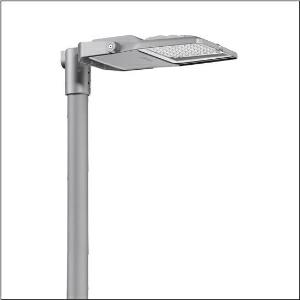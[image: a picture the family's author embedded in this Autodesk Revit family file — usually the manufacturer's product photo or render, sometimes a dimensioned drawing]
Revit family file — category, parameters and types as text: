
# Revit family: floodlight_fl_21_iq_mini___pl64_5xa7772b2e3a_76f3
name_source: partatom
category: Lighting Fixtures
units: mm (PartAtom-declared; Revit-internal decimal feet)

## family parameters
Cut with Voids When Loaded = No
Host = Face
Light Source = No
Part Type = Normal
Room Calculation Point = No
Round Connector Dimension = Use Diameter
Shared = No

## types (1)
- --- (1 x LED, 6020 lm, 45.5 W, 3000K)
    Apparent Load = 46 VA
    CIE Flux Codes = 28 80 98 100 100
    Color Rendering = 70
    Color Temperature = 3000K
    Default Elevation = 1800 mm
    Description = Floodlight FL 21 iQ mini, floodlight, primary light control with lens, of PMMA, primary optical cover: protective disc, of toughened safety glass, transparent, light distribution: PL64, light emission: direct distribution, installation type: surface-mounted, LED, High Power LED, rated luminous flux: 6.020lm, luminous efficacy: 132lm/W, light colour: 730, colour temperature: 3000K, control: Auto-Match, Temp-Guard, Night-Set, Smart-Wire, Desk-Remote (wireless, voltage-free reading and setting of iQ features in the workshop via application-optimized NFC function/RFID function), optimised constant luminous flux control (CLO 2.0), Light-Fading, Lumen-Switch, with terminal, 6-pole, mains connection: 220..240V, AC, 50/60Hz, start of lifetime: 46W, end of service life: 48W, reduction: 22W, luminaire housing, of diecast aluminium, powder-coated, Siteco® metallic grey (DB 702S), corrosivity category C5 mid according to DIN EN ISO 12944, sealing non-destructively replaceable, please order mast flange separately, mast bracket, of steel, galvanised, powder-coated, protection rating (complete): IP66, insulation class (complete): insulation class II (safety insulation), certification: CE, ENEC, VDE, protection symbol: D, impact resistance: IK08, permissible operating ambient temperature: -40..+40°C, permissible operating ambient temperature for outdoor applications: -40..+50°C, standard: DIN EN 12944, LABS conformity tested according to VDMA 24364:2018-05, packaging unit: 1 piece

Light Distribution: PL64
    Height = 70 mm
    Lamp = 1 x LED
    Lamp Light Flux = 6020 lm
    Lamp Power = 45.5 W
    Lamp count = 1
    Length = 485 mm
    Luminous efficacy = 132 lm/W
    Manufacturer = Siteco
    ModVariant = No
    Model = 5XA7772B2E3A
    Number of Poles = 1
    OnlyDefault = Yes
    Power Factor = 1
    Product Name = Floodlight FL 21 iQ mini | PL64
    Product group = floodlight | pylon annexe
    ProductGroupID = 6200
    Protection Class = Protection class II
    Protection Degree = IP 66
    RLX_Detail_Level = 1
    RLX_Emergency_Light_Flux = 0 lm
    RLX_Emergency_Type = 0
    RLX_Emergency_Type_DB = No
    RlxData = <blob elided: 101157 chars, md5=4a06a4b0>
    Socket = socket
    Standby Power = 0 W
    System Light Flux = 6020 lm
    System Power = 46 W
    Type Comments = factory setting: luminous flux: 100 % | dim-lin: 254 | 463 mA
    Type Image = l_1007125.jpg
    URL = http://relux.com
    VarID = @adj_117053
    Voltage = 0 V
    Weight = 0.00 kg
    Width = 337 mm

## geometry (parser evidence)
native form markers: Blend x4, Sweep x12
no freeform markers — native parametric forms only
